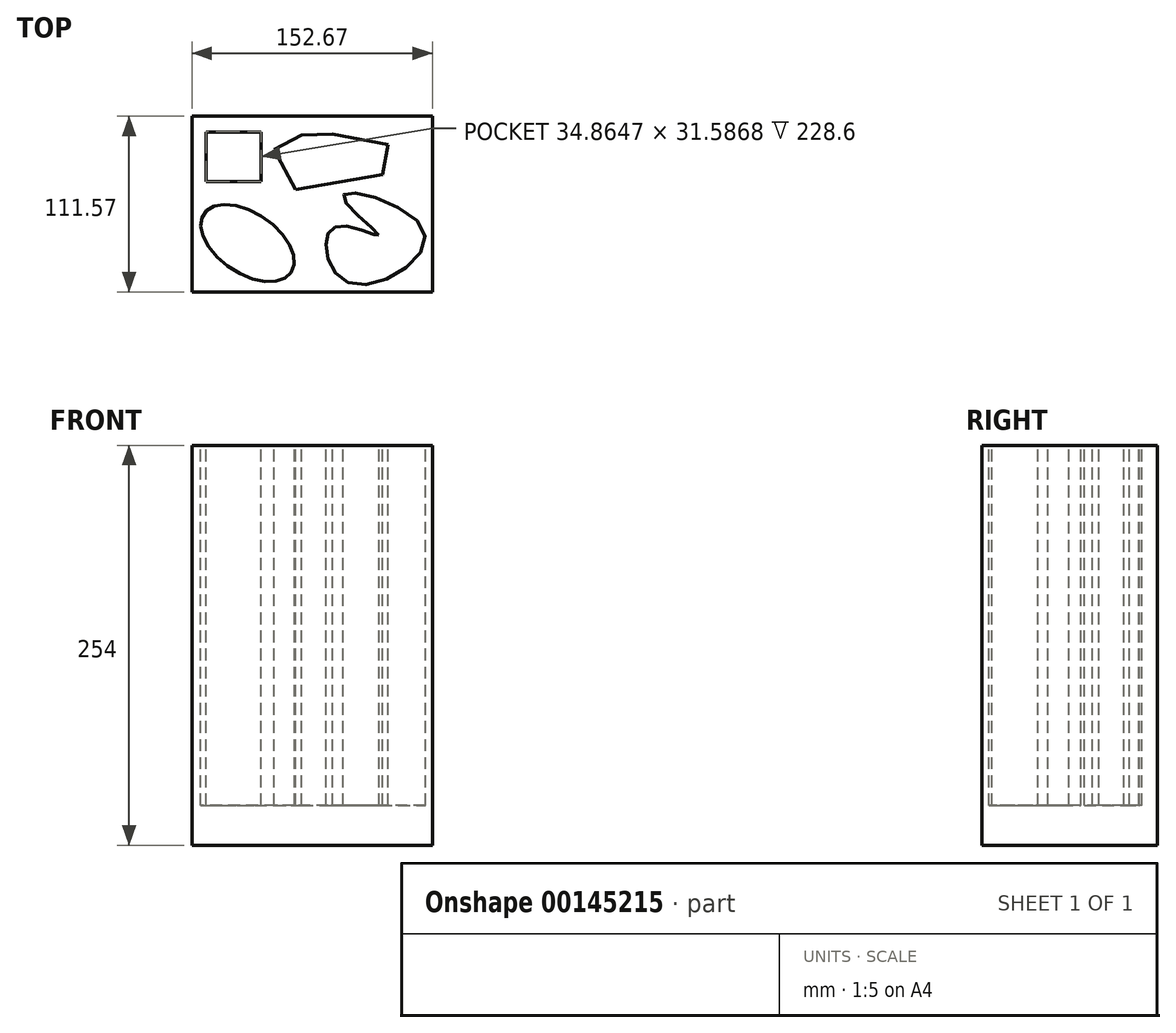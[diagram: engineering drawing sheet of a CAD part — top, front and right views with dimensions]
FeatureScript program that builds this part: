
annotation { "Feature Type Name" : "Feature", "Feature Type Description" : "" }
export const myFeature = defineFeature(function(context is Context, id is Id, definition is map)
    precondition{}
    {
        {
            var Q0;
            Q0=qCreatedBy(makeId("Top.planeOp"),FACE);
            var sketch = newSketch(context, id + "F0", { "sketchPlane" : qUnion([Q0])});
            skLineSegment(sketch, "E0.bottom", {"start": v(-76.5, 55.95) * mm, "end": v(76.17, 55.95) * mm});
            skLineSegment(sketch, "E0.top", {"start": v(-76.5, -55.62) * mm, "end": v(76.17, -55.62) * mm});
            skLineSegment(sketch, "E0.left", {"start": v(-76.5, 55.95) * mm, "end": v(-76.5, -55.62) * mm});
            skLineSegment(sketch, "E0.right", {"start": v(76.17, 55.95) * mm, "end": v(76.17, -55.62) * mm});
            skSolve(sketch);
        }
        {
            var Q0;
            Q0 = qSketchRegion(id + "F0", true);
            extrude(context, id + "F1", {"entities" : qUnion([Q0]), "depth" : 254 * mm});
        }
        {
            var Q0;
            Q0=makeQuery(id+"F1.opExtrude","CAP_FACE",FACE,{"disambiguationData":[OSD([sQuery(id+"F0.wireOp",EDGE,"E0.bottom"),sQuery(id+"F0.wireOp",EDGE,"E0.top"),sQuery(id+"F0.wireOp",EDGE,"E0.left"),sQuery(id+"F0.wireOp",EDGE,"E0.right")])],"isStart":false});
            var sketch = newSketch(context, id + "F2", { "sketchPlane" : qUnion([Q0])});
            skEllipse(sketch, "E1", {"center": v(-41.23, -24.69) * mm, "majorRadius": 33.43 * mm, "minorRadius": 19.18 * mm, "majorAxis": v(0.83, -0.56)});
            skSolve(sketch);
        }
        {
            var Q0;
            Q0 = qSketchRegion(id + "F2", true);
            extrude(context, id + "F3", {"entities" : qUnion([Q0]), "operationType" : NewBodyOperationType.REMOVE, "oppositeDirection" : true, "depth" : 228.6 * mm});
        }
        {
            var Q0;
            Q0=makeQuery(id+"F1.opExtrude","CAP_FACE",FACE,{"disambiguationData":[OSD([sQuery(id+"F0.wireOp",EDGE,"E0.bottom"),sQuery(id+"F0.wireOp",EDGE,"E0.top"),sQuery(id+"F0.wireOp",EDGE,"E0.left"),sQuery(id+"F0.wireOp",EDGE,"E0.right")])],"isStart":false});
            var sketch = newSketch(context, id + "F4", { "sketchPlane" : qUnion([Q0])});
            skSolve(sketch);
        }
        {
            var Q0;
            Q0=makeQuery(id+"F4.imprint","IMPRINT",FACE,{"disambiguationData":[TD([[makeQuery(id+"F4.imprint","IMPRINT",EDGE,{"derivedFrom":makeQuery(id+"F1.opExtrude","CAP_EDGE",EDGE,{"disambiguationData":[OSD([sQuery(id+"F0.wireOp",EDGE,"E0.bottom")])],"isStart":false})}),-1.0]])]});
            var sketch = newSketch(context, id + "F5", { "sketchPlane" : qUnion([Q0])});
            skSolve(sketch);
        }
        {
            var Q0;
            Q0=makeQuery(id+"F5.imprint","IMPRINT",FACE,{"disambiguationData":[TD([[makeQuery(id+"F5.imprint","IMPRINT",EDGE,{"derivedFrom":makeQuery(id+"F4.imprint","IMPRINT",EDGE,{"derivedFrom":makeQuery(id+"F1.opExtrude","CAP_EDGE",EDGE,{"disambiguationData":[OSD([sQuery(id+"F0.wireOp",EDGE,"E0.bottom")])],"isStart":false})})}),-1.0]])]});
            var sketch = newSketch(context, id + "F6", { "sketchPlane" : qUnion([Q0])});
            skLineSegment(sketch, "E2", {"start": v(12.66, 44.55) * mm, "end": v(48.12, 38) * mm});
            skLineSegment(sketch, "E3", {"start": v(48.12, 38) * mm, "end": v(44.59, 18.86) * mm});
            skLineSegment(sketch, "E4", {"start": v(44.59, 18.86) * mm, "end": v(-10.58, 9.39) * mm});
            skLineSegment(sketch, "E5", {"start": v(-10.58, 9.39) * mm, "end": v(-24.29, 34.72) * mm});
            skLineSegment(sketch, "E6", {"start": v(-24.29, 34.72) * mm, "end": v(-7.02, 44.06) * mm});
            skLineSegment(sketch, "E7", {"start": v(-7.02, 44.06) * mm, "end": v(12.66, 44.55) * mm});
            skSolve(sketch);
        }
        {
            var Q0;
            Q0 = qSketchRegion(id + "F6", true);
            extrude(context, id + "F7", {"entities" : qUnion([Q0]), "operationType" : NewBodyOperationType.REMOVE, "oppositeDirection" : true, "depth" : 228.6 * mm});
        }
        {
            var Q0;
            Q0=makeQuery(id+"F5.imprint","IMPRINT",FACE,{"disambiguationData":[TD([[makeQuery(id+"F5.imprint","IMPRINT",EDGE,{"derivedFrom":makeQuery(id+"F4.imprint","IMPRINT",EDGE,{"derivedFrom":makeQuery(id+"F1.opExtrude","CAP_EDGE",EDGE,{"disambiguationData":[OSD([sQuery(id+"F0.wireOp",EDGE,"E0.bottom")])],"isStart":false})})}),-1.0]])]});
            var sketch = newSketch(context, id + "F8", { "sketchPlane" : qUnion([Q0])});
            skFitSpline(sketch, "E8", {"points": [v(42.16, -19.52) * mm, v(21.6, -13.86) * mm, v(8.79, -22.5) * mm, v(26.67, -50.8) * mm, v(71.07, -17.43) * mm, v(19.52, 5.51) * mm, v(42.16, -19.52) * mm]});
            skSolve(sketch);
        }
        {
            var Q0;
            Q0 = qSketchRegion(id + "F8", true);
            extrude(context, id + "F9", {"entities" : qUnion([Q0]), "operationType" : NewBodyOperationType.REMOVE, "oppositeDirection" : true, "depth" : 228.6 * mm});
        }
        {
            var Q0;
            Q0=makeQuery(id+"F5.imprint","IMPRINT",FACE,{"disambiguationData":[TD([[makeQuery(id+"F5.imprint","IMPRINT",EDGE,{"derivedFrom":makeQuery(id+"F4.imprint","IMPRINT",EDGE,{"derivedFrom":makeQuery(id+"F1.opExtrude","CAP_EDGE",EDGE,{"disambiguationData":[OSD([sQuery(id+"F0.wireOp",EDGE,"E0.bottom")])],"isStart":false})})}),-1.0]])]});
            var sketch = newSketch(context, id + "F10", { "sketchPlane" : qUnion([Q0])});
            skLineSegment(sketch, "E9.bottom", {"start": v(-67.5, 46.04) * mm, "end": v(-32.63, 46.04) * mm});
            skLineSegment(sketch, "E9.top", {"start": v(-67.5, 14.45) * mm, "end": v(-32.63, 14.45) * mm});
            skLineSegment(sketch, "E9.left", {"start": v(-67.5, 46.04) * mm, "end": v(-67.5, 14.45) * mm});
            skLineSegment(sketch, "E9.right", {"start": v(-32.63, 46.04) * mm, "end": v(-32.63, 14.45) * mm});
            skSolve(sketch);
        }
        {
            var Q0;
            Q0 = qSketchRegion(id + "F10", true);
            extrude(context, id + "F11", {"entities" : qUnion([Q0]), "operationType" : NewBodyOperationType.REMOVE, "oppositeDirection" : true, "depth" : 228.6 * mm});
        }
    });
